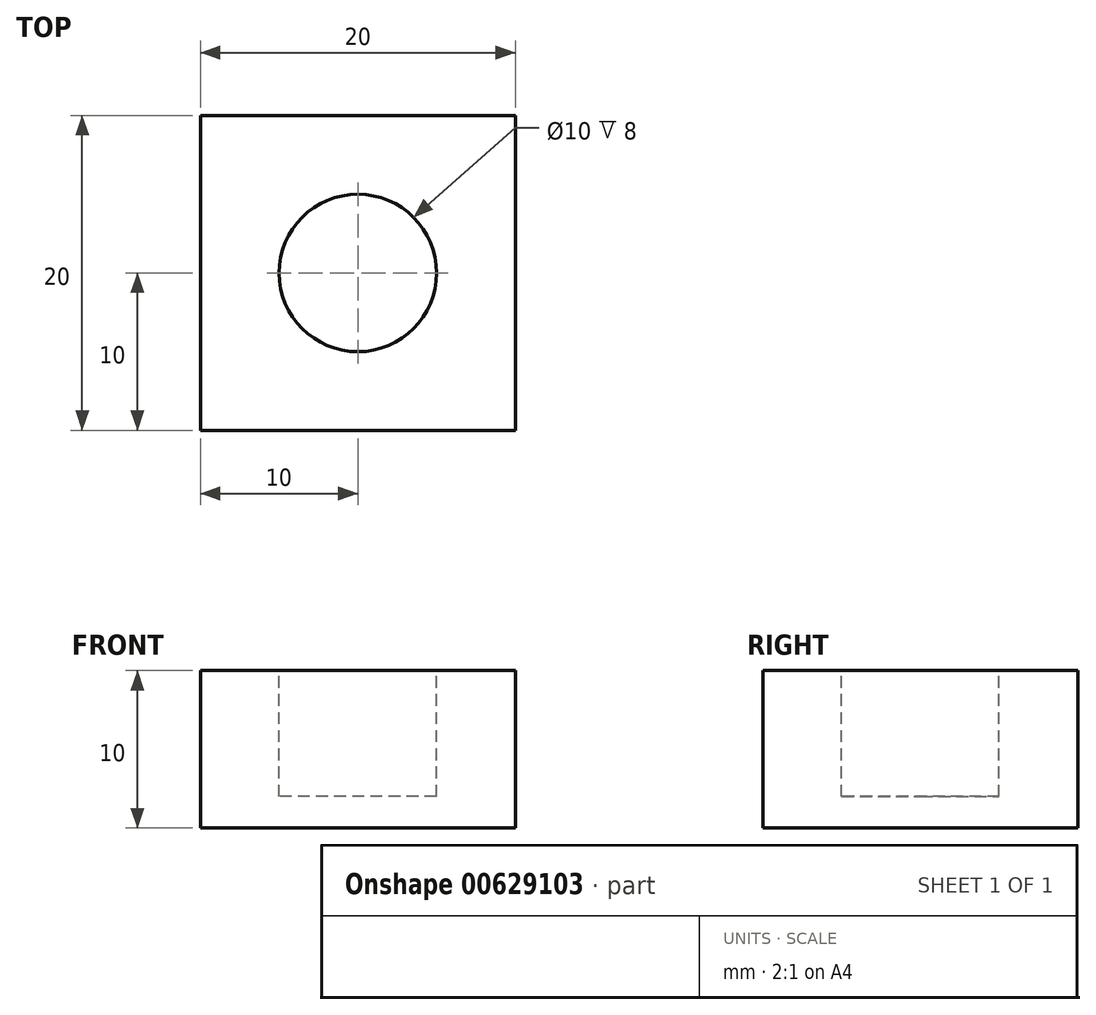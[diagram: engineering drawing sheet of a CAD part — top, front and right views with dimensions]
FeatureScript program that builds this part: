
annotation { "Feature Type Name" : "Feature", "Feature Type Description" : "" }
export const myFeature = defineFeature(function(context is Context, id is Id, definition is map)
    precondition{}
    {
        {
            var Q0;
            Q0=qCreatedBy(makeId("Top.planeOp"),FACE);
            var sketch = newSketch(context, id + "F0", { "sketchPlane" : qUnion([Q0])});
            skLineSegment(sketch, "E0.bottom", {"start": v(-10, 10) * mm, "end": v(10, 10) * mm});
            skLineSegment(sketch, "E0.top", {"start": v(-10, -10) * mm, "end": v(10, -10) * mm});
            skLineSegment(sketch, "E0.left", {"start": v(-10, 10) * mm, "end": v(-10, -10) * mm});
            skLineSegment(sketch, "E0.right", {"start": v(10, 10) * mm, "end": v(10, -10) * mm});
            skSolve(sketch);
        }
        {
            var Q0;
            Q0=makeQuery(id+"F0.imprint","IMPRINT",FACE,{"disambiguationData":[TD([[makeQuery(id+"F0.imprint","IMPRINT",EDGE,{"derivedFrom":sQuery(id+"F0.wireOp",EDGE,"E0.bottom")}),-1.0]])]});
            extrude(context, id + "F1", {"entities" : qUnion([Q0]), "depth" : 10 * mm, "offsetDistance" : 25 * mm});
        }
        {
            var Q0;
            Q0=makeQuery(id+"F1.opExtrude","CAP_FACE",FACE,{"disambiguationData":[OSD([sQuery(id+"F0.wireOp",EDGE,"E0.bottom"),sQuery(id+"F0.wireOp",EDGE,"E0.top"),sQuery(id+"F0.wireOp",EDGE,"E0.left"),sQuery(id+"F0.wireOp",EDGE,"E0.right")])],"isStart":false});
            var sketch = newSketch(context, id + "F2", { "sketchPlane" : qUnion([Q0])});
            skCircle(sketch, "E1", {"center": v(0, 0) * mm, "radius": 5 * mm});
            skSolve(sketch);
        }
        {
            var Q0;
            Q0 = qSketchRegion(id + "F2", true);
            extrude(context, id + "F3", {"entities" : qUnion([Q0]), "operationType" : NewBodyOperationType.REMOVE, "oppositeDirection" : true, "depth" : 8 * mm, "offsetDistance" : 25 * mm});
        }
    });
